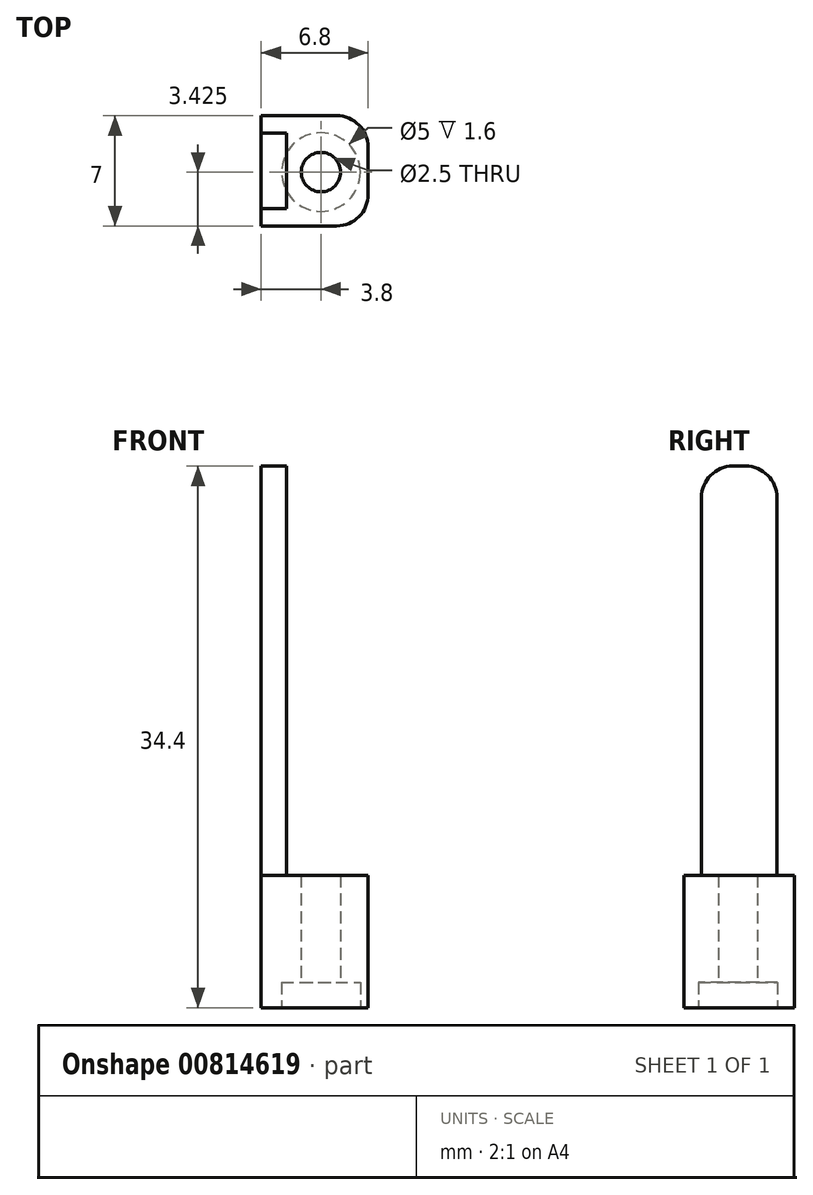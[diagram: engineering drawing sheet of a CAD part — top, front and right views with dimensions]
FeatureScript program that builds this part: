
annotation { "Feature Type Name" : "Feature", "Feature Type Description" : "" }
export const myFeature = defineFeature(function(context is Context, id is Id, definition is map)
    precondition{}
    {
        {
            var Q0;
            Q0=qCreatedBy(makeId("Top.planeOp"),FACE);
            var sketch = newSketch(context, id + "F0", { "sketchPlane" : qUnion([Q0])});
            skLineSegment(sketch, "E0.bottom", {"start": v(-4, 21.81) * mm, "end": v(1, 21.81) * mm});
            skLineSegment(sketch, "E0.top", {"start": v(-4, 14.81) * mm, "end": v(1, 14.81) * mm});
            skLineSegment(sketch, "E0.left", {"start": v(3, 16.81) * mm, "end": v(3, 19.81) * mm});
            skLineSegment(sketch, "E0.right", {"start": v(-4, 14.81) * mm, "end": v(-4, 21.81) * mm});
            skPoint(sketch, "E1.visualSharp", {"position": v(3, 21.81) * mm});
            skArc(sketch, "E1.filletArc", {"start": v(3, 19.81) * mm, "mid": v(2.41, 21.23) * mm, "end": v(1, 21.81) * mm});
            skPoint(sketch, "E2.visualSharp", {"position": v(3, 14.81) * mm});
            skArc(sketch, "E2.filletArc", {"start": v(1, 14.81) * mm, "mid": v(2.41, 15.4) * mm, "end": v(3, 16.81) * mm});
            skSolve(sketch);
        }
        {
            var Q0;
            Q0=makeQuery(id+"F0.imprint","IMPRINT",FACE,{"disambiguationData":[TD([[makeQuery(id+"F0.imprint","IMPRINT",EDGE,{"derivedFrom":sQuery(id+"F0.wireOp",EDGE,"E0.bottom")}),-1.0]])]});
            var Q1;
            Q1=makeQuery(id+"F0.imprint","IMPRINT",FACE,{"disambiguationData":[TD([[makeQuery(id+"F0.imprint","IMPRINT",EDGE,{"derivedFrom":sQuery(id+"F0.wireOp",EDGE,"OGHk75Aa-BJnh-hkSo-yNRI-ETdDBhqNUhSb")}),1.0]])]});
            var Q2;
            Q2=makeQuery(id+"F0.imprint","IMPRINT",FACE,{"disambiguationData":[TD([[makeQuery(id+"F0.imprint","IMPRINT",EDGE,{"derivedFrom":sQuery(id+"F0.wireOp",EDGE,"Jd6CkG7M-QaOW-uCvP-q8XN-jmcHcbD0AcgO")}),1.0]])]});
            extrude(context, id + "F1", {"entities" : qUnion([Q0, Q1, Q2]), "depth" : 8.4 * mm, "offsetDistance" : 25 * mm});
        }
        {
            var Q0;
            Q0=makeQuery(id+"F1.opExtrude","CAP_FACE",FACE,{"disambiguationData":[OSD([sQuery(id+"F0.wireOp",EDGE,"E0.bottom"),sQuery(id+"F0.wireOp",EDGE,"E0.top"),sQuery(id+"F0.wireOp",EDGE,"E0.left"),sQuery(id+"F0.wireOp",EDGE,"E0.right"),sQuery(id+"F0.wireOp",EDGE,"E1.filletArc"),sQuery(id+"F0.wireOp",EDGE,"E2.filletArc")])],"isStart":true});
            var sketch = newSketch(context, id + "F2", { "sketchPlane" : qUnion([Q0])});
            skCircle(sketch, "E3", {"center": v(0, -18.23) * mm, "radius": 2.5 * mm});
            skSolve(sketch);
        }
        {
            var Q0;
            Q0=qSketchRegion(id+"F2",true);
            extrude(context, id + "F3", {"entities" : qUnion([Q0]), "operationType" : NewBodyOperationType.REMOVE, "oppositeDirection" : true, "depth" : 1.6 * mm, "offsetDistance" : 25 * mm});
        }
        {
            var Q0;
            Q0=makeQuery(id+"F3.boolean.opBoolean","COPY",FACE,{"derivedFrom":makeQuery(id+"F3.opExtrude","CAP_FACE",FACE,{"disambiguationData":[OSD([sQuery(id+"F2.wireOp",EDGE,"E3")])],"isStart":false})});
            var sketch = newSketch(context, id + "F4", { "sketchPlane" : qUnion([Q0])});
            skCircle(sketch, "E4", {"center": v(0, -18.23) * mm, "radius": 1.25 * mm});
            skSolve(sketch);
        }
        {
            var Q0;
            Q0=qSketchRegion(id+"F4",true);
            extrude(context, id + "F5", {"entities" : qUnion([Q0]), "operationType" : NewBodyOperationType.REMOVE, "oppositeDirection" : true, "depth" : 10 * mm, "offsetDistance" : 25 * mm});
        }
        {
            var Q0;
            Q0=makeQuery(id+"F1.opExtrude","CAP_FACE",FACE,{"disambiguationData":[OSD([sQuery(id+"F0.wireOp",EDGE,"E0.bottom"),sQuery(id+"F0.wireOp",EDGE,"E0.top"),sQuery(id+"F0.wireOp",EDGE,"E0.left"),sQuery(id+"F0.wireOp",EDGE,"E0.right"),sQuery(id+"F0.wireOp",EDGE,"E1.filletArc"),sQuery(id+"F0.wireOp",EDGE,"E2.filletArc")])],"isStart":false});
            var sketch = newSketch(context, id + "F6", { "sketchPlane" : qUnion([Q0])});
            skLineSegment(sketch, "E5.bottom", {"start": v(-4, 20.71) * mm, "end": v(-2, 20.71) * mm});
            skLineSegment(sketch, "E5.top", {"start": v(-4, 15.91) * mm, "end": v(-2, 15.91) * mm});
            skLineSegment(sketch, "E5.left", {"start": v(-4, 20.71) * mm, "end": v(-4, 15.91) * mm});
            skLineSegment(sketch, "E5.right", {"start": v(-2, 20.71) * mm, "end": v(-2, 15.91) * mm});
            skSolve(sketch);
        }
        {
            var Q0;
            Q0=qSketchRegion(id+"F6",true);
            extrude(context, id + "F7", {"entities" : qUnion([Q0]), "operationType" : NewBodyOperationType.ADD, "depth" : 26 * mm, "offsetDistance" : 25 * mm});
        }
        {
            var Q0;
            Q0=makeQuery(id+"F7.opExtrude","CAP_EDGE",EDGE,{"disambiguationData":[OSD([sQuery(id+"F6.wireOp",EDGE,"E5.bottom")])],"isStart":false});
            var Q1;
            Q1=makeQuery(id+"F7.opExtrude","CAP_EDGE",EDGE,{"disambiguationData":[OSD([sQuery(id+"F6.wireOp",EDGE,"E5.top")])],"isStart":false});
            fillet(context, id + "F8", {"entities" : qUnion([Q0, Q1]), "radius" : 2 * mm, "tangentPropagation" : true, "allowEdgeOverflow" : false});
        }
        {
            var Q0;
            Q0=makeQuery(id+"F7.opExtrude","SWEPT_FACE",FACE,{"disambiguationData":[OSD([sQuery(id+"F6.wireOp",EDGE,"E5.right")])]});
            extrude(context, id + "F9", {"entities" : qUnion([Q0]), "operationType" : NewBodyOperationType.REMOVE, "oppositeDirection" : true, "depth" : 0.2 * mm, "offsetDistance" : 25 * mm});
        }
        {
            var Q0;
            Q0=makeQuery(id+"F7.boolean.opBoolean","MERGE",FACE,{"derivedFrom":[makeQuery(id+"F1.opExtrude","SWEPT_FACE",FACE,{"disambiguationData":[OSD([sQuery(id+"F0.wireOp",EDGE,"E0.right")])]}),makeQuery(id+"F7.opExtrude","SWEPT_FACE",FACE,{"disambiguationData":[OSD([sQuery(id+"F6.wireOp",EDGE,"E5.left")])]})]});
            extrude(context, id + "F10", {"entities" : qUnion([Q0]), "operationType" : NewBodyOperationType.REMOVE, "oppositeDirection" : true, "depth" : 0.2 * mm, "offsetDistance" : 25 * mm});
        }
    });
